# Revit family: 11STERN_SOAP_DISPENSER_TOUCHLESS_CSABA
name_source: partatom
category: Generic Models
revit_build: Autodesk Revit 2017 (Build: 20160225_1515(x64)
units: mm (PartAtom-declared; Revit-internal decimal feet)

## family parameters
Can host rebar = No
Cut with Voids When Loaded = No
Host = Face
Part Type = Normal
Room Calculation Point = Yes
Round Connector Dimension = Use Diameter
Shared = No

## types (2) — shared parameters
AVAILABLE FINISHES = Brushed Nickel - Matt Black - Satin Gold - PVD Antique Bronze - PVD rose Gold - PVD Copper - AISI316 Material
BADGE = https://bim.archiproducts.com
Default Elevation = 1219 mm
Description = CSABA Soap Dispenser - Touch free electronic soap dispenser for deck mounted installations.‎ Activated by infrared sensor.‎ Chrome plated body, other finishes available.‎  Includes a 1 liter soap bottle and bottle support.‎ Optional for remote installation: extension cable and longer piping.‎ The following functions can be performed by using Stern remote control: soap quantity selection, refill the soap tank, temporary off, coming back to factory settings.‎
FINISHING MATERIAL = Chrome - Stern
INSTALLATION = Deck mounted
MATERIAL DESCRIPTION = Finish: Chrome
Manufacturer = Stern Engineering
OPTIONS = Remote control (code 07100008), Matching battery-powered faucet (code 233000), Matching transformer-powered faucet (code 233010), 6-Pack: 6 soap dispensers and a remote control (upon request), Multifeed system (upon request)
PRODUCT SHEET = https://www.archiproducts.com
REFILL = Easy to use refill buttom in order will start to come out of the soap dispenser spout. This function can also be performed with the remote control.
SOAP = 1 Liter soap bottle. This soap dispenser incluses a peristaltic pump that allows the use of any kind of liquind soap, detergent or antibacterial gel.
SOAP DOSE = Factory setting for 0.7 to 0.9 cc depending on the selected soap. The soap quantity can be changed using the soap dispenser's remote control
TECHNICAL SHEET = http://www.sternfaucets.com
URL = http://www.sternfaucets.com
VOLTAGE = 12 V

## per-type parameters (varying)
| type | DEPTH | HEIGHT | Model | POWER SUPPLY | PRODUCT CODE | WIDTH |
| SWAN_SD - 12V BATTERY | 122 mm | 210 mm | Csaba Soap Dispenser B | Battery box for 6 x DD batteries | 233111 | 50 mm  [stored 0.164042 ft] |
| SWAN_SD - 12V TRANSFORMER | 155 mm | 118 mm | Csaba Soap Dispenser E | 12V transformer | 233101 | 55 mm  [stored 0.180446 ft] |

note: [stored X ft] marks values corroborated as IEEE doubles in the binary element streams (Revit-internal decimal feet)

## geometry (parser evidence)
native form markers: Blend x4, Sweep x1
no freeform markers — native parametric forms only
